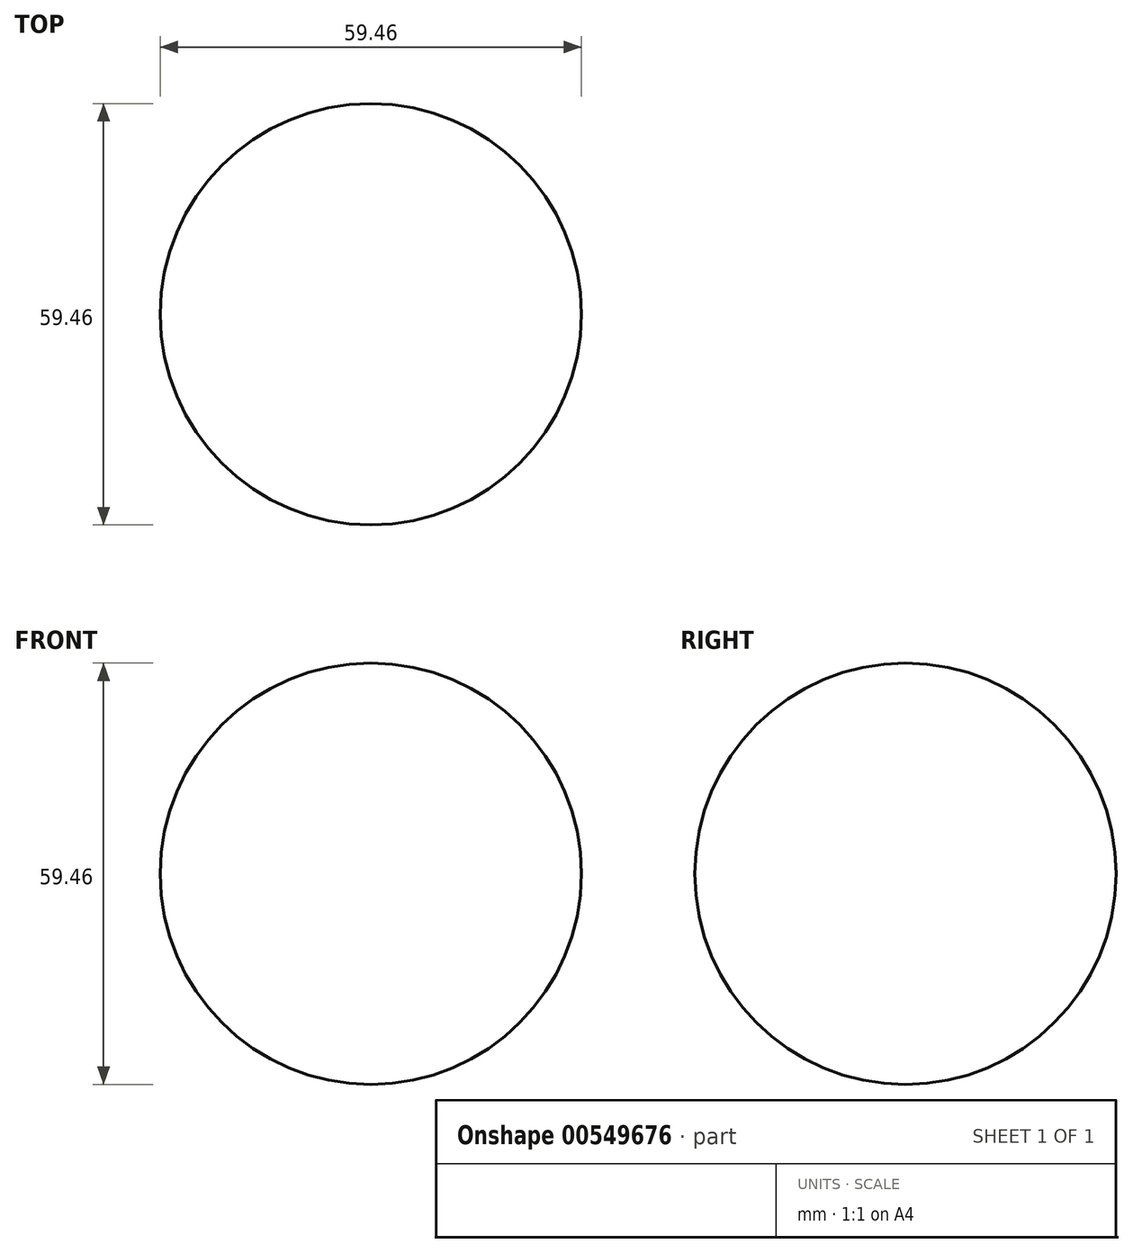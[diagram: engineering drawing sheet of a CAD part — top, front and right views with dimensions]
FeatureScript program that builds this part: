
annotation { "Feature Type Name" : "Feature", "Feature Type Description" : "" }
export const myFeature = defineFeature(function(context is Context, id is Id, definition is map)
    precondition{}
    {
        {
            var Q0;
            Q0=qCreatedBy(makeId("Front.planeOp"),FACE);
            var sketch = newSketch(context, id + "F0", { "sketchPlane" : qUnion([Q0])});
            skArc(sketch, "E0", {"start": v(0, -29.73) * mm, "mid": v(29.73, 0) * mm, "end": v(0, 29.73) * mm});
            skLineSegment(sketch, "E1", {"start": v(0, 29.73) * mm, "end": v(0, -29.73) * mm});
            skSolve(sketch);
        }
        {
            var Q0;
            Q0 = qSketchRegion(id + "F0", true);
            var Q1;
            Q1=sQuery(id+"F0.wireOp",EDGE,"E1");
            revolve(context, id + "F1", {"entities" : qUnion([Q0]), "axis" : qUnion([Q1]), "revolveType" : RevolveType.FULL});
        }
    });
